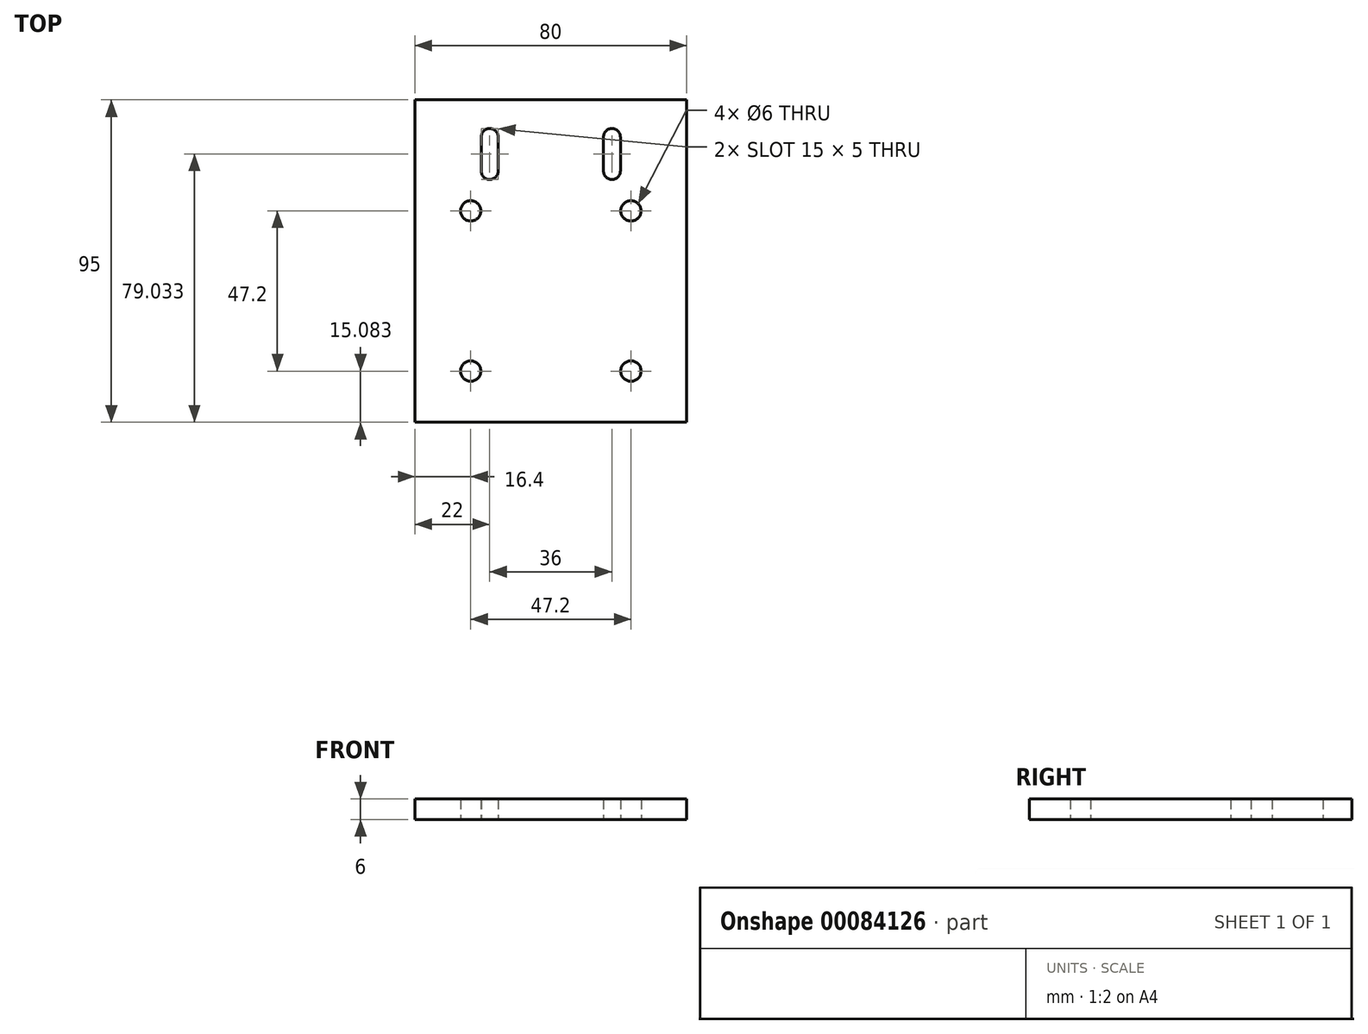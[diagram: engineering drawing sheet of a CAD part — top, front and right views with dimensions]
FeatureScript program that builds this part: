
annotation { "Feature Type Name" : "Feature", "Feature Type Description" : "" }
export const myFeature = defineFeature(function(context is Context, id is Id, definition is map)
    precondition{}
    {
        {
            var Q0;
            Q0=qCreatedBy(makeId("Top.planeOp"),FACE);
            var sketch = newSketch(context, id + "F0", { "sketchPlane" : qUnion([Q0])});
            skLineSegment(sketch, "E0.bottom", {"start": v(40, -47.5) * mm, "end": v(-40, -47.5) * mm});
            skLineSegment(sketch, "E0.top", {"start": v(40, 47.5) * mm, "end": v(-40, 47.5) * mm});
            skLineSegment(sketch, "E0.left", {"start": v(40, -47.5) * mm, "end": v(40, 47.5) * mm});
            skLineSegment(sketch, "E0.right", {"start": v(-40, -47.5) * mm, "end": v(-40, 47.5) * mm});
            skPoint(sketch, "E0.middle", {"position": v(0, 0) * mm});
            skLineSegment(sketch, "E1", {"start": v(0, -47.5) * mm, "end": v(0, 47.5) * mm, "construction": true});
            skLineSegment(sketch, "E2.bottom", {"start": v(23.6, -32.42) * mm, "end": v(-23.6, -32.42) * mm, "construction": true});
            skLineSegment(sketch, "E2.top", {"start": v(23.6, 14.78) * mm, "end": v(-23.6, 14.78) * mm, "construction": true});
            skLineSegment(sketch, "E2.left", {"start": v(23.6, -32.42) * mm, "end": v(23.6, 14.78) * mm, "construction": true});
            skLineSegment(sketch, "E2.right", {"start": v(-23.6, -32.42) * mm, "end": v(-23.6, 14.78) * mm, "construction": true});
            skPoint(sketch, "E2.middle", {"position": v(0, -8.82) * mm});
            skCircle(sketch, "E3", {"center": v(-23.6, -32.42) * mm, "radius": 3 * mm});
            skCircle(sketch, "E4", {"center": v(-23.6, 14.78) * mm, "radius": 3 * mm});
            skCircle(sketch, "E5", {"center": v(23.6, 14.78) * mm, "radius": 3 * mm});
            skCircle(sketch, "E6", {"center": v(23.6, -32.42) * mm, "radius": 3 * mm});
            skLineSegment(sketch, "E7.bottom", {"start": v(18, 26.53) * mm, "end": v(-18, 26.53) * mm, "construction": true});
            skLineSegment(sketch, "E7.top", {"start": v(18, 36.53) * mm, "end": v(-18, 36.53) * mm, "construction": true});
            skLineSegment(sketch, "E7.left", {"start": v(18, 26.53) * mm, "end": v(18, 36.53) * mm, "construction": true});
            skLineSegment(sketch, "E7.right", {"start": v(-18, 26.53) * mm, "end": v(-18, 36.53) * mm, "construction": true});
            skPoint(sketch, "E7.middle", {"position": v(0, 31.53) * mm});
            skArc(sketch, "E8", {"start": v(-15.5, 36.53) * mm, "mid": v(-18, 39.03) * mm, "end": v(-20.5, 36.53) * mm});
            skArc(sketch, "E9", {"start": v(-20.5, 26.53) * mm, "mid": v(-18, 24.03) * mm, "end": v(-15.5, 26.53) * mm});
            skArc(sketch, "E10", {"start": v(15.5, 26.53) * mm, "mid": v(18, 24.03) * mm, "end": v(20.5, 26.53) * mm});
            skArc(sketch, "E11", {"start": v(20.5, 36.53) * mm, "mid": v(18, 39.03) * mm, "end": v(15.5, 36.53) * mm});
            skLineSegment(sketch, "E12", {"start": v(-20.5, 36.53) * mm, "end": v(-20.5, 26.53) * mm});
            skLineSegment(sketch, "E13", {"start": v(-15.5, 36.53) * mm, "end": v(-15.5, 26.53) * mm});
            skLineSegment(sketch, "E14", {"start": v(15.5, 36.53) * mm, "end": v(15.5, 26.53) * mm});
            skLineSegment(sketch, "E15", {"start": v(20.5, 36.53) * mm, "end": v(20.5, 26.53) * mm});
            skSolve(sketch);
        }
        {
            var Q0;
            Q0=makeQuery(id+"F0.imprint","IMPRINT",FACE,{"disambiguationData":[TD([[makeQuery(id+"F0.imprint","IMPRINT",EDGE,{"derivedFrom":sQuery(id+"F0.wireOp",EDGE,"E0.bottom")}),-1.0]])]});
            extrude(context, id + "F1", {"entities" : qUnion([Q0]), "depth" : 6 * mm});
        }
    });
